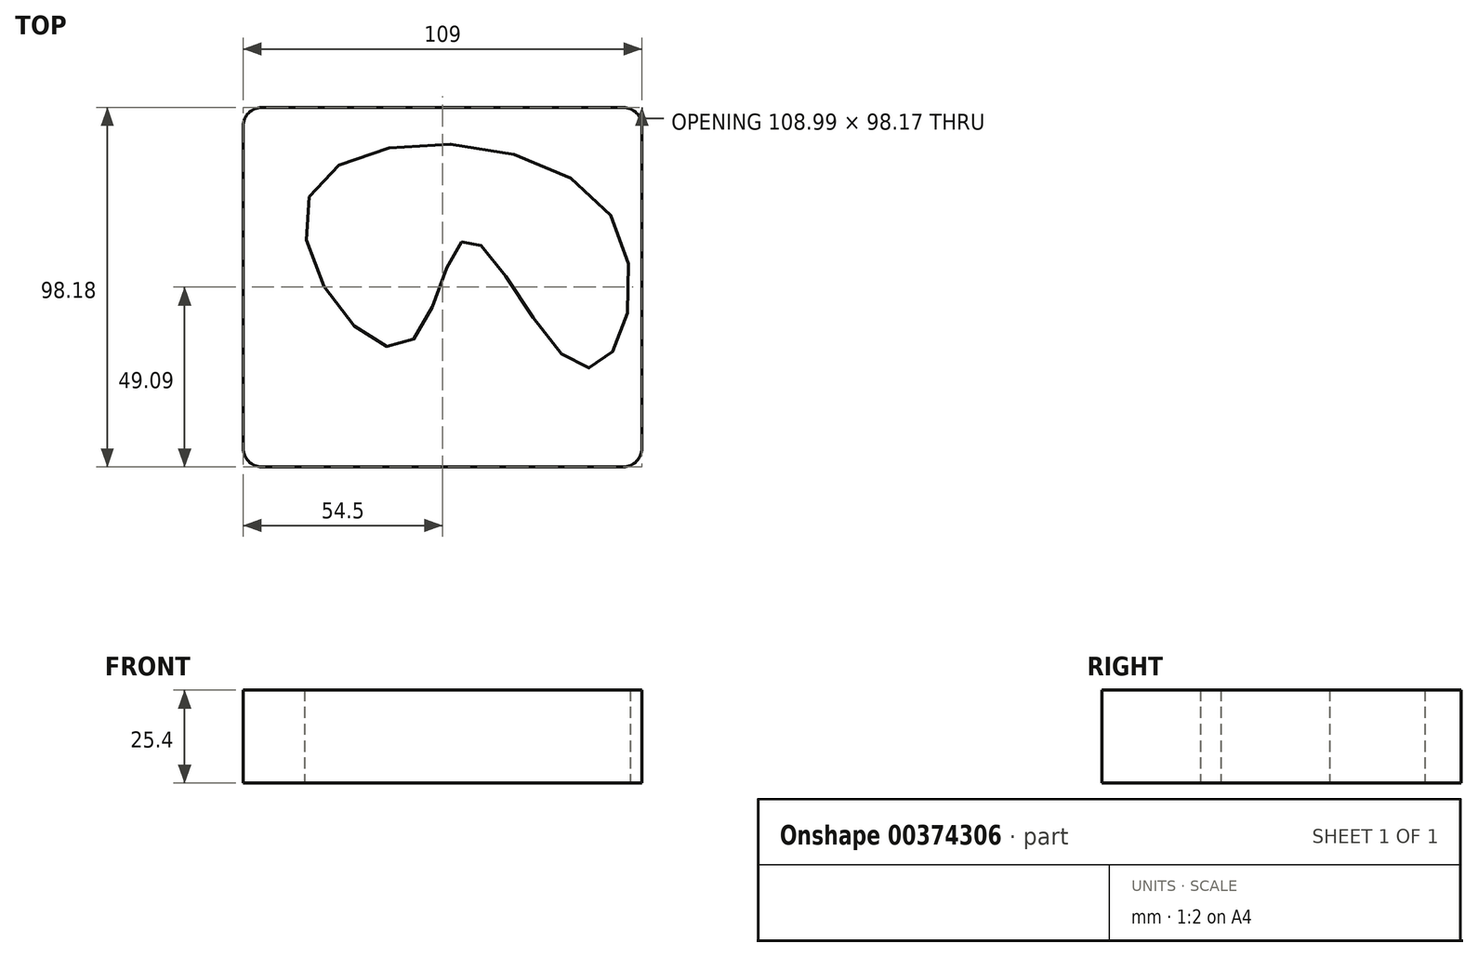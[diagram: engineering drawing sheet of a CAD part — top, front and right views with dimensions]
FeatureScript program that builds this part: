
annotation { "Feature Type Name" : "Feature", "Feature Type Description" : "" }
export const myFeature = defineFeature(function(context is Context, id is Id, definition is map)
    precondition{}
    {
        {
            var Q0;
            Q0=qCreatedBy(makeId("Top.planeOp"),FACE);
            var sketch = newSketch(context, id + "F0", { "sketchPlane" : qUnion([Q0])});
            skLineSegment(sketch, "E0.bottom", {"start": v(54.5, 49.09) * mm, "end": v(-54.5, 49.09) * mm});
            skLineSegment(sketch, "E0.top", {"start": v(54.5, -49.09) * mm, "end": v(-54.5, -49.09) * mm});
            skLineSegment(sketch, "E0.left", {"start": v(54.5, 49.09) * mm, "end": v(54.5, -49.09) * mm});
            skLineSegment(sketch, "E0.right", {"start": v(-54.5, 49.09) * mm, "end": v(-54.5, -49.09) * mm});
            skPoint(sketch, "E0.middle", {"position": v(0, 0) * mm});
            skSolve(sketch);
        }
        {
            var Q0;
            Q0 = qSketchRegion(id + "F0", true);
            extrude(context, id + "F1", {"entities" : qUnion([Q0]), "depth" : 25.4 * mm});
        }
        {
            var Q0;
            Q0=makeQuery(id+"F1.opExtrude","SWEPT_EDGE",EDGE,{"disambiguationData":[OSD([sQuery(id+"F0.wireOp",EDGE,"E0.top"),sQuery(id+"F0.wireOp",EDGE,"E0.left")])]});
            var Q1;
            Q1=makeQuery(id+"F1.opExtrude","SWEPT_EDGE",EDGE,{"disambiguationData":[OSD([sQuery(id+"F0.wireOp",EDGE,"E0.bottom"),sQuery(id+"F0.wireOp",EDGE,"E0.left")])]});
            var Q2;
            Q2=makeQuery(id+"F1.opExtrude","SWEPT_EDGE",EDGE,{"disambiguationData":[OSD([sQuery(id+"F0.wireOp",EDGE,"E0.bottom"),sQuery(id+"F0.wireOp",EDGE,"E0.right")])]});
            var Q3;
            Q3=makeQuery(id+"F1.opExtrude","SWEPT_EDGE",EDGE,{"disambiguationData":[OSD([sQuery(id+"F0.wireOp",EDGE,"E0.top"),sQuery(id+"F0.wireOp",EDGE,"E0.right")])]});
            fillet(context, id + "F2", {"entities" : qUnion([Q0, Q1, Q2, Q3]), "radius" : 5.08 * mm, "tangentPropagation" : true, "allowEdgeOverflow" : false});
        }
        {
            var Q0;
            Q0=makeQuery(id+"F1.opExtrude","CAP_FACE",FACE,{"disambiguationData":[OSD([sQuery(id+"F0.wireOp",EDGE,"E0.bottom"),sQuery(id+"F0.wireOp",EDGE,"E0.top"),sQuery(id+"F0.wireOp",EDGE,"E0.left"),sQuery(id+"F0.wireOp",EDGE,"E0.right")])],"isStart":false});
            var sketch = newSketch(context, id + "F3", { "sketchPlane" : qUnion([Q0])});
            skFitSpline(sketch, "E1", {"points": [v(-36.48, 24.72) * mm, v(-11.04, -16.29) * mm, v(6.89, 13.1) * mm, v(38.81, -22.05) * mm, v(44.98, 21) * mm, v(-36.48, 24.72) * mm]});
            skSolve(sketch);
        }
        {
            var Q0;
            Q0=makeQuery(id+"F3.imprint","IMPRINT",FACE,{"disambiguationData":[TD([[makeQuery(id+"F3.imprint","IMPRINT",EDGE,{"derivedFrom":sQuery(id+"F3.wireOp",EDGE,"E1")}),1.0]])]});
            extrude(context, id + "F4", {"entities" : qUnion([Q0]), "operationType" : NewBodyOperationType.REMOVE, "endBound" : BoundingType.THROUGH_ALL, "oppositeDirection" : true, "depth" : 25.4 * mm});
        }
    });
